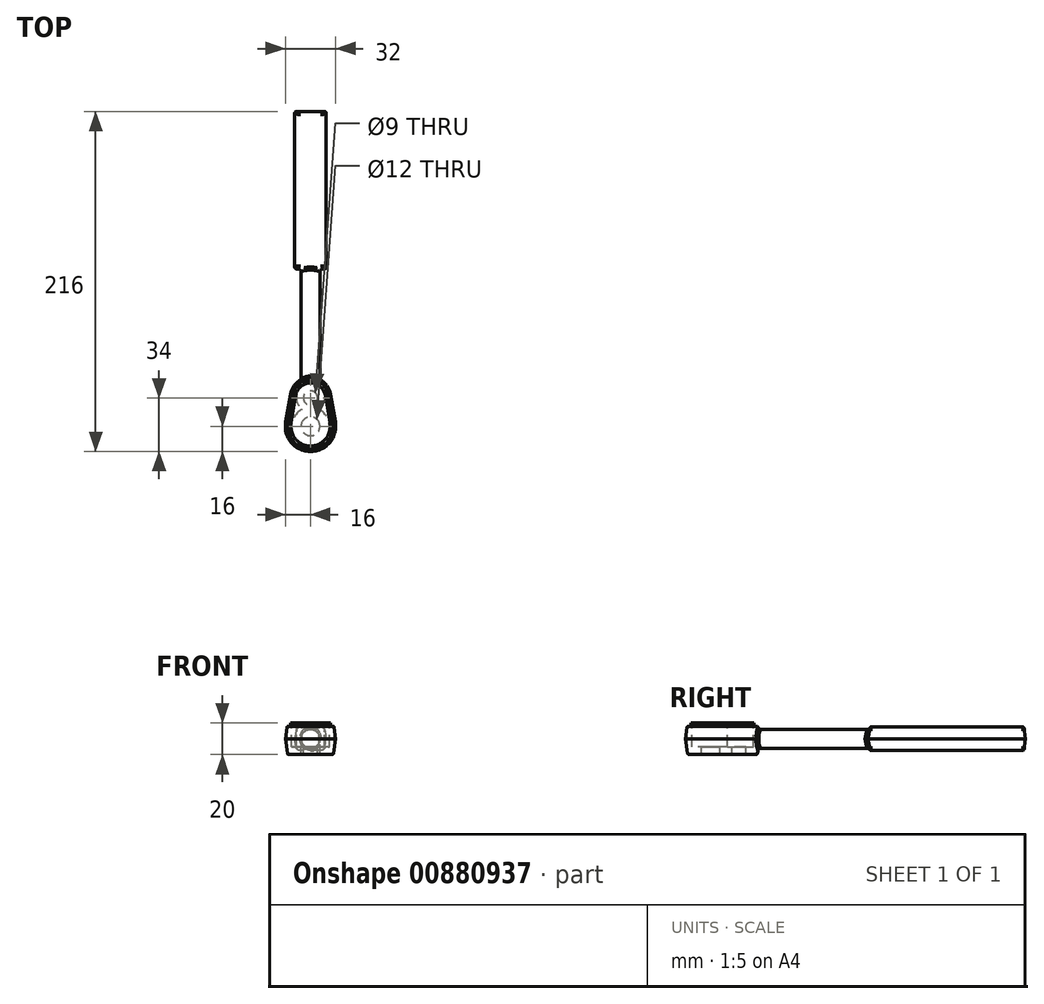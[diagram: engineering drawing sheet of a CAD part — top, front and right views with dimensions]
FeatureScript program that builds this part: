
annotation { "Feature Type Name" : "Feature", "Feature Type Description" : "" }
export const myFeature = defineFeature(function(context is Context, id is Id, definition is map)
    precondition{}
    {
        {
            var Q0;
            Q0=qCreatedBy(makeId("Top.planeOp"),FACE);
            var sketch = newSketch(context, id + "F0", { "sketchPlane" : qUnion([Q0])});
            skLineSegment(sketch, "E0", {"start": v(0, 148.55) * mm, "end": v(0, 0) * mm, "construction": true});
            skLineSegment(sketch, "E1", {"start": v(0, 200) * mm, "end": v(10, 200) * mm});
            skLineSegment(sketch, "E2", {"start": v(10, 200) * mm, "end": v(10, 100) * mm});
            skLineSegment(sketch, "E3", {"start": v(10, 100) * mm, "end": v(0, 100) * mm});
            skLineSegment(sketch, "E4.MirrorCS", {"start": v(0, 200) * mm, "end": v(-10, 200) * mm});
            skLineSegment(sketch, "E5.MirrorCS", {"start": v(-10, 100) * mm, "end": v(0, 100) * mm});
            skLineSegment(sketch, "E6.MirrorCS", {"start": v(-10, 200) * mm, "end": v(-10, 100) * mm});
            skSolve(sketch);
        }
        {
            var Q0;
            Q0=makeQuery(id+"F0.imprint","IMPRINT",FACE,{"disambiguationData":[TD([[makeQuery(id+"F0.imprint","IMPRINT",EDGE,{"derivedFrom":sQuery(id+"F0.wireOp",EDGE,"E1")}),-1.0]])]});
            extrude(context, id + "F1", {"entities" : qUnion([Q0]), "endBound" : BoundingType.SYMMETRIC, "depth" : 15 * mm, "offsetDistance" : 25 * mm, "hasDraft" : true, "draftAngle" : 8 * degree, "draftPullDirection" : true});
        }
        {
            var Q0;
            Q0=qCreatedBy(makeId("Front.planeOp"),FACE);
            var sketch = newSketch(context, id + "F2", { "sketchPlane" : qUnion([Q0])});
            skCircle(sketch, "E7", {"center": v(0, 0) * mm, "radius": 6 * mm});
            skSolve(sketch);
        }
        {
            var Q0;
            Q0=makeQuery(id+"F2.imprint","IMPRINT",FACE,{"disambiguationData":[TD([[makeQuery(id+"F2.imprint","IMPRINT",EDGE,{"derivedFrom":sQuery(id+"F2.wireOp",EDGE,"E7")}),1.0]])]});
            var Q1;
            Q1=sQuery(id+"F2.wireOp",EDGE,"E7");
            extrude(context, id + "F3", {"entities" : qUnion([Q0]), "operationType" : NewBodyOperationType.ADD, "surfaceEntities" : qUnion([Q1]), "endBound" : BoundingType.UP_TO_NEXT, "oppositeDirection" : true, "depth" : 25 * mm, "offsetDistance" : 25 * mm});
        }
        {
            var Q0;
            Q0=qCreatedBy(makeId("Top.planeOp"),FACE);
            var sketch = newSketch(context, id + "F4", { "sketchPlane" : qUnion([Q0])});
            skLineSegment(sketch, "E8", {"start": v(-15.78, 2.67) * mm, "end": v(-12.82, 20.17) * mm});
            skArc(sketch, "E9", {"start": v(-12.82, 20.17) * mm, "mid": v(0, 31) * mm, "end": v(12.82, 20.17) * mm});
            skLineSegment(sketch, "E10", {"start": v(12.82, 20.17) * mm, "end": v(15.78, 2.67) * mm});
            skArc(sketch, "E11", {"start": v(15.78, 2.67) * mm, "mid": v(0, -16) * mm, "end": v(-15.78, 2.67) * mm});
            skSolve(sketch);
        }
        {
            var Q0;
            Q0=makeQuery(id+"F4.imprint","IMPRINT",FACE,{"disambiguationData":[TD([[makeQuery(id+"F4.imprint","IMPRINT",EDGE,{"derivedFrom":sQuery(id+"F4.wireOp",EDGE,"E8")}),-1.0]])]});
            extrude(context, id + "F5", {"entities" : qUnion([Q0]), "operationType" : NewBodyOperationType.ADD, "endBound" : BoundingType.SYMMETRIC, "oppositeDirection" : true, "depth" : 20 * mm, "offsetDistance" : 25 * mm, "hasDraft" : true, "draftAngle" : 8 * degree, "draftPullDirection" : true});
        }
        {
            var Q0;
            Q0=makeQuery(id+"F5.opExtrude","CAP_FACE",FACE,{"disambiguationData":[OSD([sQuery(id+"F4.wireOp",EDGE,"E8"),sQuery(id+"F4.wireOp",EDGE,"E9"),sQuery(id+"F4.wireOp",EDGE,"E10"),sQuery(id+"F4.wireOp",EDGE,"E11")])],"isStart":true});
            var sketch = newSketch(context, id + "F6", { "sketchPlane" : qUnion([Q0])});
            skArc(sketch, "E12.0", {"start": v(12.42, 2.1) * mm, "mid": v(0, -12.6) * mm, "end": v(-12.42, 2.1) * mm});
            skLineSegment(sketch, "E12.1", {"start": v(9.46, 19.6) * mm, "end": v(12.42, 2.1) * mm});
            skArc(sketch, "E12.2", {"start": v(-9.46, 19.6) * mm, "mid": v(0, 27.6) * mm, "end": v(9.46, 19.6) * mm});
            skLineSegment(sketch, "E12.3", {"start": v(-12.42, 2.1) * mm, "end": v(-9.46, 19.6) * mm});
            skSolve(sketch);
        }
        {
            var Q0;
            Q0=makeQuery(id+"F6.imprint","IMPRINT",FACE,{"disambiguationData":[TD([[makeQuery(id+"F6.imprint","IMPRINT",EDGE,{"derivedFrom":sQuery(id+"F6.wireOp",EDGE,"E12.0")}),-1.0]])]});
            extrude(context, id + "F7", {"entities" : qUnion([Q0]), "operationType" : NewBodyOperationType.REMOVE, "oppositeDirection" : true, "depth" : 2 * mm, "offsetDistance" : 25 * mm});
        }
        {
            var Q0;
            Q0=makeQuery(id+"F7.boolean.opBoolean","COPY",FACE,{"derivedFrom":makeQuery(id+"F7.opExtrude","CAP_FACE",FACE,{"disambiguationData":[OSD([sQuery(id+"F6.wireOp",EDGE,"E12.0"),sQuery(id+"F6.wireOp",EDGE,"E12.1"),sQuery(id+"F6.wireOp",EDGE,"E12.2"),sQuery(id+"F6.wireOp",EDGE,"E12.3")])],"isStart":false})});
            var sketch = newSketch(context, id + "F8", { "sketchPlane" : qUnion([Q0])});
            skArc(sketch, "E13", {"start": v(-5.33, 10.75) * mm, "mid": v(0, -12) * mm, "end": v(5.33, 10.75) * mm});
            skArc(sketch, "E14", {"start": v(5.33, 10.75) * mm, "mid": v(0, 27) * mm, "end": v(-5.33, 10.75) * mm});
            skSolve(sketch);
        }
        {
            var Q0;
            Q0 = qSketchRegion(id + "F8", true);
            extrude(context, id + "F9", {"entities" : qUnion([Q0]), "operationType" : NewBodyOperationType.REMOVE, "endBound" : BoundingType.UP_TO_NEXT, "oppositeDirection" : true, "depth" : 25 * mm, "hasOffset" : true, "offsetDistance" : 5 * mm});
        }
        {
            var Q0;
            Q0=makeQuery(id+"F9.boolean.opBoolean","COPY",FACE,{"derivedFrom":makeQuery(id+"F9.opExtrude","CAP_FACE",FACE,{"disambiguationData":[OSD([sQuery(id+"F8.wireOp",EDGE,"E13"),sQuery(id+"F8.wireOp",EDGE,"E14")])],"isStart":false})});
            var sketch = newSketch(context, id + "F10", { "sketchPlane" : qUnion([Q0])});
            skCircle(sketch, "E15", {"center": v(0, 18) * mm, "radius": 4.5 * mm});
            skSolve(sketch);
        }
        {
            var Q0;
            Q0 = qSketchRegion(id + "F10", true);
            extrude(context, id + "F11", {"entities" : qUnion([Q0]), "operationType" : NewBodyOperationType.REMOVE, "endBound" : BoundingType.THROUGH_ALL, "oppositeDirection" : true, "depth" : 25 * mm, "offsetDistance" : 25 * mm});
        }
        {
            var Q0;
            Q0=makeQuery(id+"F9.boolean.opBoolean","COPY",FACE,{"derivedFrom":makeQuery(id+"F9.opExtrude","CAP_FACE",FACE,{"disambiguationData":[OSD([sQuery(id+"F8.wireOp",EDGE,"E13"),sQuery(id+"F8.wireOp",EDGE,"E14")])],"isStart":false})});
            var sketch = newSketch(context, id + "F12", { "sketchPlane" : qUnion([Q0])});
            skCircle(sketch, "E16", {"center": v(0, 0) * mm, "radius": 6 * mm});
            skSolve(sketch);
        }
        {
            var Q0;
            Q0 = qSketchRegion(id + "F12", true);
            extrude(context, id + "F13", {"entities" : qUnion([Q0]), "operationType" : NewBodyOperationType.REMOVE, "endBound" : BoundingType.THROUGH_ALL, "oppositeDirection" : true, "depth" : 25 * mm, "offsetDistance" : 25 * mm});
        }
        {
            var Q0;
            Q0=makeQuery(id+"F1.opExtrude","CAP_EDGE",EDGE,{"disambiguationData":[OSD([sQuery(id+"F0.wireOp",EDGE,"E2")])],"isStart":false});
            var Q1;
            Q1=makeQuery(id+"F1.opExtrude","CAP_EDGE",EDGE,{"disambiguationData":[OSD([sQuery(id+"F0.wireOp",EDGE,"E6.MirrorCS")])],"isStart":false});
            var Q2;
            Q2=makeQuery(id+"F1.opExtrude","CAP_EDGE",EDGE,{"disambiguationData":[OSD([sQuery(id+"F0.wireOp",EDGE,"E2")])],"isStart":true});
            var Q3;
            Q3=makeQuery(id+"F1.opExtrude","CAP_EDGE",EDGE,{"disambiguationData":[OSD([sQuery(id+"F0.wireOp",EDGE,"E6.MirrorCS")])],"isStart":true});
            fillet(context, id + "F14", {"entities" : qUnion([Q0, Q1, Q2, Q3]), "radius" : 3 * mm, "tangentPropagation" : true, "allowEdgeOverflow" : false});
        }
        {
            var Q0;
            Q0=makeQuery(id+"F1.opExtrude","CAP_EDGE",EDGE,{"disambiguationData":[OSD([sQuery(id+"F0.wireOp",EDGE,"E3"),sQuery(id+"F0.wireOp",EDGE,"E5.MirrorCS")])],"isStart":false});
            var Q1;
            Q1=makeQuery(id+"F1.opExtrude","CAP_EDGE",EDGE,{"disambiguationData":[OSD([sQuery(id+"F0.wireOp",EDGE,"E1"),sQuery(id+"F0.wireOp",EDGE,"E4.MirrorCS")])],"isStart":false});
            var Q2;
            Q2=makeQuery(id+"F1.opExtrude","CAP_EDGE",EDGE,{"disambiguationData":[OSD([sQuery(id+"F0.wireOp",EDGE,"E1"),sQuery(id+"F0.wireOp",EDGE,"E4.MirrorCS")])],"isStart":true});
            var Q3;
            Q3=makeQuery(id+"F1.opExtrude","CAP_EDGE",EDGE,{"disambiguationData":[OSD([sQuery(id+"F0.wireOp",EDGE,"E3"),sQuery(id+"F0.wireOp",EDGE,"E5.MirrorCS")])],"isStart":true});
            var Q4;
            Q4=makeQuery(id+"F5.opExtrude","CAP_EDGE",EDGE,{"disambiguationData":[OSD([sQuery(id+"F4.wireOp",EDGE,"E11")])],"isStart":true});
            var Q5;
            Q5=makeQuery(id+"F5.opExtrude","CAP_EDGE",EDGE,{"disambiguationData":[OSD([sQuery(id+"F4.wireOp",EDGE,"E11")])],"isStart":false});
            fillet(context, id + "F15", {"entities" : qUnion([Q0, Q1, Q2, Q3, Q4, Q5]), "radius" : 1 * mm, "tangentPropagation" : true, "allowEdgeOverflow" : false});
        }
        {
            var Q0;
            Q0=makeQuery(id+"F3.opExtrude","SWEPT_FACE",FACE,{"disambiguationData":[OSD([sQuery(id+"F2.wireOp",EDGE,"E7")])]});
            fillet(context, id + "F16", {"entities" : qUnion([Q0]), "radius" : 2 * mm, "tangentPropagation" : true, "allowEdgeOverflow" : false});
        }
    });
